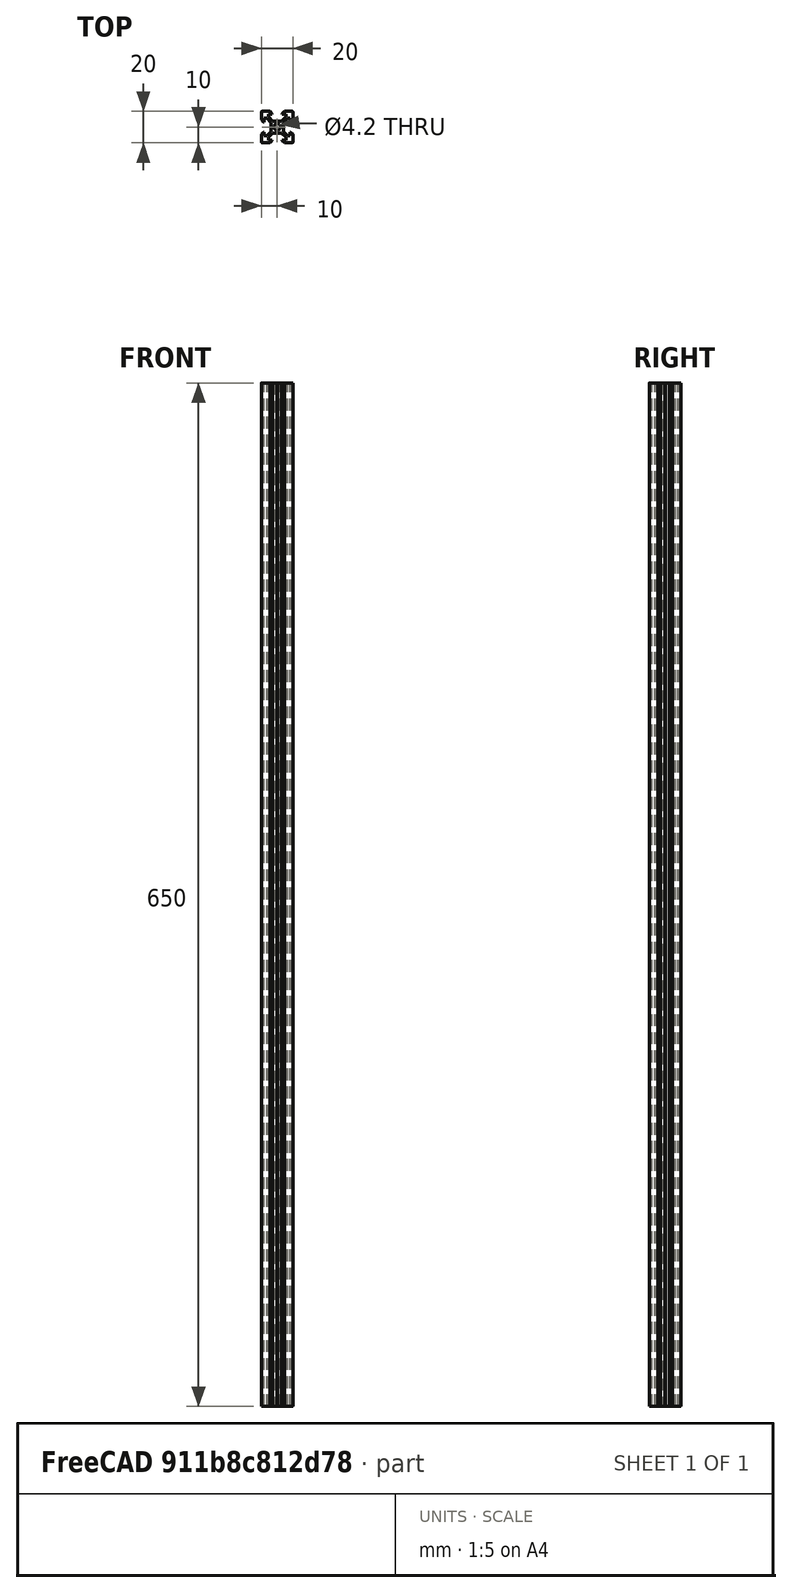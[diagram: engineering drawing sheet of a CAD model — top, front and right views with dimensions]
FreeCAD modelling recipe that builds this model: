
FCSTD DOCUMENT  (FreeCAD 0.19R)
Label: 2020-650
License: All rights reserved
LicenseURL: http://en.wikipedia.org/wiki/All_rights_reserved
objects: Sketcher::SketchObject×1, PartDesign::Pad×1, PartDesign::Body×1
note: 4 computed .brp shape members not serialized (recipe doc carries the construction recipe); baked Part::Feature solids carry a one-line shape summary decoded from their .brp

FEATURE [Sketcher::SketchObject] Sketch
  FullyConstrained = true
  MapMode = 5
  Support = -> [XY_Plane]
  sketch-geometry (65):
    g0: LineSegment StartX=-10 StartY=4.58 StartZ=0 EndX=-10 EndY=9.5 EndZ=0
    g1: LineSegment StartX=-9.5 StartY=10 StartZ=0 EndX=-4.58 EndY=10 EndZ=0
    g2: LineSegment StartX=-5.5 StartY=8.2 StartZ=0 EndX=-3.125 EndY=8.2 EndZ=0
    g3: LineSegment StartX=-8.2 StartY=5.5 StartZ=0 EndX=-8.2 EndY=3.125 EndZ=0
    g4: LineSegment StartX=-0.125 StartY=3.9 StartZ=0 EndX=-2.83934 EndY=3.9 EndZ=0
    g5: LineSegment StartX=-3.9 StartY=2.83934 StartZ=0 EndX=-3.9 EndY=0.125 EndZ=0
    g6: ArcOfCircle CenterX=0 CenterY=3.9 CenterZ=0 NormalX=0 NormalY=0 NormalZ=1 AngleXU=0 Radius=0.125 StartAngle=3.14159 EndAngle=6.28319
    g7: ArcOfCircle CenterX=-3.9 CenterY=0 CenterZ=0 NormalX=0 NormalY=0 NormalZ=1 AngleXU=0 Radius=0.125 StartAngle=4.71239 EndAngle=7.85398
    g8: ArcOfCircle CenterX=-9.5 CenterY=9.5 CenterZ=0 NormalX=0 NormalY=0 NormalZ=1 AngleXU=0 Radius=0.5 StartAngle=1.5708 EndAngle=3.14159
    g9: LineSegment StartX=-5.5 StartY=8.2 StartZ=0 EndX=-5.5 EndY=6.56066 EndZ=0
    g10: LineSegment StartX=-8.2 StartY=5.5 StartZ=0 EndX=-6.56066 EndY=5.5 EndZ=0
    g11: LineSegment StartX=-4.58 StartY=10 StartZ=0 EndX=-3.125 EndY=8.545 EndZ=0
    g12: LineSegment StartX=-3.125 StartY=8.545 StartZ=0 EndX=-3.125 EndY=8.2 EndZ=0
    g13: LineSegment StartX=-10 StartY=4.58 StartZ=0 EndX=-8.545 EndY=3.125 EndZ=0
    g14: LineSegment StartX=-8.545 StartY=3.125 StartZ=0 EndX=-8.2 EndY=3.125 EndZ=0
    g15: LineSegment StartX=-5.5 StartY=6.56066 StartZ=0 EndX=-2.83934 EndY=3.9 EndZ=0
    g16: LineSegment StartX=-6.56066 StartY=5.5 StartZ=0 EndX=-3.9 EndY=2.83934 EndZ=0
    g17: Circle CenterX=0 CenterY=0 CenterZ=0 NormalX=0 NormalY=0 NormalZ=1 AngleXU=0 Radius=2.1
    g18: LineSegment StartX=0.125 StartY=3.9 StartZ=0 EndX=2.83934 EndY=3.9 EndZ=0
    g19: LineSegment StartX=2.83934 StartY=3.9 StartZ=0 EndX=5.5 EndY=6.56066 EndZ=0
    g20: LineSegment StartX=5.5 StartY=6.56066 StartZ=0 EndX=5.5 EndY=8.2 EndZ=0
    g21: LineSegment StartX=3.125 StartY=8.2 StartZ=0 EndX=3.125 EndY=8.545 EndZ=0
    g22: LineSegment StartX=5.5 StartY=8.2 StartZ=0 EndX=3.125 EndY=8.2 EndZ=0
    g23: LineSegment StartX=4.58 StartY=10 StartZ=0 EndX=9.5 EndY=10 EndZ=0
    g24: ArcOfCircle CenterX=9.5 CenterY=9.5 CenterZ=0 NormalX=0 NormalY=0 NormalZ=1 AngleXU=0 Radius=0.5 StartAngle=1.9e-15 EndAngle=1.5708
    g25: LineSegment StartX=10 StartY=9.5 StartZ=0 EndX=10 EndY=4.58 EndZ=0
    g26: LineSegment StartX=10 StartY=4.58 StartZ=0 EndX=8.545 EndY=3.125 EndZ=0
    g27: LineSegment StartX=8.545 StartY=3.125 StartZ=0 EndX=8.2 EndY=3.125 EndZ=0
    g28: LineSegment StartX=8.2 StartY=3.125 StartZ=0 EndX=8.2 EndY=5.5 EndZ=0
    g29: LineSegment StartX=8.2 StartY=5.5 StartZ=0 EndX=6.56066 EndY=5.5 EndZ=0
    g30: LineSegment StartX=6.56066 StartY=5.5 StartZ=0 EndX=3.9 EndY=2.83934 EndZ=0
    g31: LineSegment StartX=3.9 StartY=2.83934 StartZ=0 EndX=3.9 EndY=0.125 EndZ=0
    g32: ArcOfCircle CenterX=3.9 CenterY=0 CenterZ=0 NormalX=0 NormalY=0 NormalZ=1 AngleXU=0 Radius=0.125 StartAngle=1.5708 EndAngle=4.71239
    g33: LineSegment StartX=3.9 StartY=-0.125 StartZ=0 EndX=3.9 EndY=-2.83934 EndZ=0
    g34: LineSegment StartX=3.9 StartY=-2.83934 StartZ=0 EndX=6.56066 EndY=-5.5 EndZ=0
    g35: LineSegment StartX=6.56066 StartY=-5.5 StartZ=0 EndX=8.2 EndY=-5.5 EndZ=0
    g36: LineSegment StartX=8.2 StartY=-5.5 StartZ=0 EndX=8.2 EndY=-3.125 EndZ=0
    g37: LineSegment StartX=8.2 StartY=-3.125 StartZ=0 EndX=8.545 EndY=-3.125 EndZ=0
    g38: LineSegment StartX=8.545 StartY=-3.125 StartZ=0 EndX=10 EndY=-4.58 EndZ=0
    g39: LineSegment StartX=10 StartY=-4.58 StartZ=0 EndX=10 EndY=-9.5 EndZ=0
    g40: ArcOfCircle CenterX=9.5 CenterY=-9.5 CenterZ=0 NormalX=0 NormalY=0 NormalZ=1 AngleXU=0 Radius=0.5 StartAngle=4.71239 EndAngle=6.28319
    g41: LineSegment StartX=9.5 StartY=-10 StartZ=0 EndX=4.58 EndY=-10 EndZ=0
    g42: LineSegment StartX=4.58 StartY=-10 StartZ=0 EndX=3.125 EndY=-8.545 EndZ=0
    g43: LineSegment StartX=2.83934 StartY=-3.9 StartZ=0 EndX=5.5 EndY=-6.56066 EndZ=0
    g44: LineSegment StartX=3.125 StartY=-8.545 StartZ=0 EndX=3.125 EndY=-8.2 EndZ=0
    g45: LineSegment StartX=3.125 StartY=-8.2 StartZ=0 EndX=5.5 EndY=-8.2 EndZ=0
    g46: LineSegment StartX=5.5 StartY=-8.2 StartZ=0 EndX=5.5 EndY=-6.56066 EndZ=0
    g47: ArcOfCircle CenterX=0 CenterY=-3.9 CenterZ=0 NormalX=0 NormalY=0 NormalZ=1 AngleXU=0 Radius=0.125 StartAngle=0 EndAngle=3.14159
    g48: LineSegment StartX=0.125 StartY=-3.9 StartZ=0 EndX=2.83934 EndY=-3.9 EndZ=0
    g49: LineSegment StartX=-0.125 StartY=-3.9 StartZ=0 EndX=-2.83934 EndY=-3.9 EndZ=0
    g50: LineSegment StartX=-3.9 StartY=-0.125 StartZ=0 EndX=-3.9 EndY=-2.83934 EndZ=0
    g51: LineSegment StartX=-3.9 StartY=-2.83934 StartZ=0 EndX=-6.56066 EndY=-5.5 EndZ=0
    g52: LineSegment StartX=-6.56066 StartY=-5.5 StartZ=0 EndX=-8.2 EndY=-5.5 EndZ=0
    g53: LineSegment StartX=-8.2 StartY=-5.5 StartZ=0 EndX=-8.2 EndY=-3.125 EndZ=0
    g54: LineSegment StartX=-8.2 StartY=-3.125 StartZ=0 EndX=-8.545 EndY=-3.125 EndZ=0
    g55: LineSegment StartX=-8.545 StartY=-3.125 StartZ=0 EndX=-10 EndY=-4.58 EndZ=0
    g56: LineSegment StartX=-10 StartY=-4.58 StartZ=0 EndX=-10 EndY=-9.5 EndZ=0
    g57: ArcOfCircle CenterX=-9.5 CenterY=-9.5 CenterZ=0 NormalX=0 NormalY=0 NormalZ=1 AngleXU=0 Radius=0.5 StartAngle=3.14159 EndAngle=4.71239
    g58: LineSegment StartX=-9.5 StartY=-10 StartZ=0 EndX=-4.58 EndY=-10 EndZ=0
    g59: LineSegment StartX=-4.58 StartY=-10 StartZ=0 EndX=-3.125 EndY=-8.545 EndZ=0
    g60: LineSegment StartX=-2.83934 StartY=-3.9 StartZ=0 EndX=-5.5 EndY=-6.56066 EndZ=0
    g61: LineSegment StartX=-5.5 StartY=-6.56066 StartZ=0 EndX=-5.5 EndY=-8.2 EndZ=0
    g62: LineSegment StartX=-5.5 StartY=-8.2 StartZ=0 EndX=-3.125 EndY=-8.2 EndZ=0
    g63: LineSegment StartX=-3.125 StartY=-8.545 StartZ=0 EndX=-3.125 EndY=-8.2 EndZ=0
    g64: LineSegment StartX=3.125 StartY=8.545 StartZ=0 EndX=4.58 EndY=10 EndZ=0
  constraints (194):
    c: Diameter(g17) = 4.2
    c: Radius(g32) = 0.125
    c: Coincident(g-1,g17)
    c: DistanceY(g57,g1) = 20
    c: DistanceX(g56,g39) = 20
    c: Radius(g57) = 0.5
    c: DistanceX(g56,g17) = 10
    c: DistanceY(g57,g17) = 10
    c: Distance(g5,g4) = 1.5
    c: DistanceY(g20,g23) = 1.8
    c: DistanceY(g18,g20) = 4.3
    c: DistanceX(g11,g21) = 6.25
    c: DistanceX(g1,g23) = 9.16
    c: DistanceX(g2,g20) = 11
    c: Coincident(g6,g18)
    c: Coincident(g6,g4)
    c: Coincident(g4,g15)
    c: Coincident(g18,g19)
    c: Coincident(g5,g16)
    c: Coincident(g16,g10)
    c: Coincident(g15,g9)
    c: Coincident(g12,g2)
    c: Coincident(g2,g9)
    c: Coincident(g12,g11)
    c: Coincident(g1,g11)
    c: Coincident(g23,g64)
    c: Coincident(g22,g21)
    c: Coincident(g64,g21)
    c: Coincident(g22,g20)
    c: Coincident(g19,g20)
    c: Coincident(g25,g26)
    c: Coincident(g27,g26)
    c: Coincident(g27,g28)
    c: Coincident(g28,g29)
    c: Coincident(g29,g30)
    c: Coincident(g0,g13)
    c: Coincident(g14,g13)
    c: Coincident(g14,g3)
    c: Coincident(g3,g10)
    c: Coincident(g5,g7)
    c: Coincident(g50,g7)
    c: Coincident(g51,g50)
    c: Coincident(g52,g51)
    c: Coincident(g52,g53)
    c: Coincident(g54,g53)
    c: Coincident(g55,g54)
    c: Coincident(g56,g55)
    c: Coincident(g58,g59)
    c: Coincident(g63,g59)
    c: Coincident(g62,g63)
    c: Coincident(g62,g61)
    c: Coincident(g60,g61)
    c: Coincident(g49,g60)
    c: Coincident(g47,g49)
    c: Coincident(g48,g47)
    c: Coincident(g48,g43)
    c: Coincident(g46,g43)
    c: Coincident(g45,g46)
    c: Coincident(g45,g44)
    c: Coincident(g42,g44)
    c: Coincident(g41,g42)
    c: Coincident(g39,g38)
    c: Coincident(g38,g37)
    c: Coincident(g37,g36)
    c: Coincident(g35,g36)
    c: Coincident(g34,g35)
    c: Coincident(g34,g33)
    c: Coincident(g31,g30)
    c: Coincident(g33,g32)
    c: Coincident(g32,g31)
    c: Vertical(g0)
    c: Horizontal(g1)
    c: Equal(g0,g1)
    c: Horizontal(g4)
    c: PointOnObject(g6,g-2)
    c: Horizontal(g18)
    c: Horizontal(g4,g6)
    c: Horizontal(g6,g6)
    c: Parallel(g13,g11)
    c: Horizontal(g14)
    c: Vertical(g12)
    c: Equal(g14,g12)
    c: Vertical(g3)
    c: Horizontal(g2)
    c: Equal(g3,g2)
    c: Equal(g10,g9)
    c: Horizontal(g10)
    c: Vertical(g9)
    c: Parallel(g16,g15)
    c: Equal(g13,g11)
    c: Tangent(g8,g0) = 1.5708
    c: PointOnObject(g7,g-1)
    c: Vertical(g5)
    c: Vertical(g50)
    c: Vertical(g7,g7)
    c: Vertical(g7,g5)
    c: Horizontal(g52)
    c: Vertical(g53)
    c: Horizontal(g54)
    c: Vertical(g56)
    c: Equal(g50,g5)
    c: Equal(g51,g16)
    c: Perpendicular(g16,g51)
    c: Equal(g52,g10)
    c: Equal(g53,g3)
    c: Equal(g54,g14)
    c: Equal(g55,g13)
    c: Perpendicular(g55,g13)
    c: Equal(g56,g0)
    c: Tangent(g57,g56) = -1.5708
    c: Tangent(g57,g58) = -1.5708
    c: Tangent(g8,g1) = 1.5708
    c: Equal(g57,g8)
    c: Horizontal(g58)
    c: Equal(g58,g56)
    c: Equal(g55,g59)
    c: Parallel(g55,g59)
    c: Vertical(g63)
    c: Equal(g63,g54)
    c: Horizontal(g62)
    c: Vertical(g61)
    c: Equal(g61,g52)
    c: Equal(g60,g51)
    c: Parallel(g60,g51)
    c: PointOnObject(g47,g-2)
    c: Horizontal(g47,g47)
    c: Horizontal(g47,g47)
    c: Horizontal(g49)
    c: Equal(g49,g50)
    c: Horizontal(g48)
    c: Vertical(g46)
    c: Perpendicular(g60,g43)
    c: Equal(g43,g60)
    c: Equal(g46,g61)
    c: Horizontal(g45)
    c: Equal(g45,g62)
    c: Vertical(g44)
    c: Equal(g44,g63)
    c: Perpendicular(g42,g59)
    c: Equal(g42,g59)
    c: Horizontal(g41)
    c: Equal(g58,g41)
    c: Tangent(g40,g41) = 1.5708
    c: Tangent(g40,g39) = 1.5708
    c: Equal(g57,g40)
    c: Vertical(g39)
    c: Equal(g41,g39)
    c: Parallel(g42,g38)
    c: Equal(g42,g38)
    c: Horizontal(g37)
    c: Equal(g44,g37)
    c: Vertical(g36)
    c: Equal(g45,g36)
    c: Horizontal(g35)
    c: Equal(g35,g46)
    c: Parallel(g43,g34)
    c: Equal(g43,g34)
    c: PointOnObject(g32,g-1)
    c: Vertical(g33)
    c: Vertical(g32,g31)
    c: Vertical(g31,g32)
    c: Equal(g48,g33)
    c: Equal(g47,g7)
    c: Equal(g7,g6)
    c: Vertical(g31)
    c: Equal(g33,g31)
    c: Equal(g4,g5)
    c: Equal(g4,g18)
    c: Parallel(g30,g19)
    c: Equal(g30,g19)
    c: Horizontal(g29)
    c: Vertical(g20)
    c: Equal(g35,g29)
    c: Equal(g29,g20)
    c: Horizontal(g22)
    c: Equal(g22,g2)
    c: Vertical(g21)
    c: Equal(g11,g64)
    c: Horizontal(g23)
    c: Equal(g1,g23)
    c: Vertical(g28)
    c: Equal(g28,g36)
    c: Horizontal(g27)
    c: Equal(g27,g37)
    c: Perpendicular(g38,g26)
    c: Equal(g38,g26)
    c: Vertical(g25)
    c: Equal(g39,g25)
    c: Tangent(g24,g23) = 1.5708
    c: Tangent(g24,g25) = 1.5708
    c: Vertical(g25,g38)
    c: Horizontal(g2,g21)
    c: Vertical(g10,g51)
    c: Angle(g64,g11) = 1.5708
FEATURE [PartDesign::Pad] Pad
  Direction = (1,1,1)
  Length = 650
  Length2 = 100
  Profile = -> Sketch
  Type = 0
FEATURE [PartDesign::Body] Body  label="2020-650"
  Group = -> [Sketch,Pad]
  Origin = -> Origin
  Tip = -> Pad
